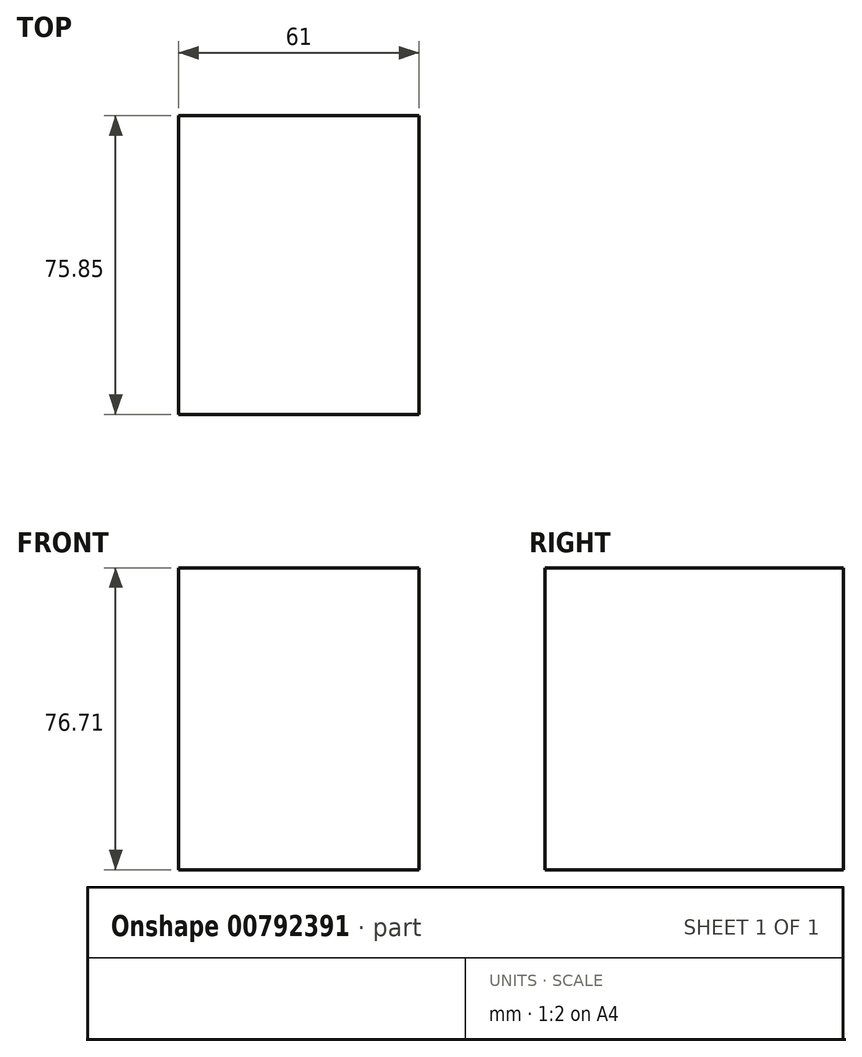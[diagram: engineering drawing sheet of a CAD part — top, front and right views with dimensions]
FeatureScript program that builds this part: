
annotation { "Feature Type Name" : "Feature", "Feature Type Description" : "" }
export const myFeature = defineFeature(function(context is Context, id is Id, definition is map)
    precondition{}
    {
        {
            var Q0;
            Q0=qCreatedBy(makeId("Top.planeOp"),FACE);
            var sketch = newSketch(context, id + "F0", { "sketchPlane" : qUnion([Q0])});
            skLineSegment(sketch, "E0.bottom", {"start": v(-26.76, -31.6) * mm, "end": v(34.24, -31.6) * mm});
            skLineSegment(sketch, "E0.top", {"start": v(-26.76, 44.24) * mm, "end": v(34.24, 44.24) * mm});
            skLineSegment(sketch, "E0.left", {"start": v(-26.76, -31.6) * mm, "end": v(-26.76, 44.24) * mm});
            skLineSegment(sketch, "E0.right", {"start": v(34.24, -31.6) * mm, "end": v(34.24, 44.24) * mm});
            skSolve(sketch);
        }
        {
            var Q0;
            Q0=makeQuery(id+"F0.imprint","IMPRINT",FACE,{"disambiguationData":[TD([[makeQuery(id+"F0.imprint","IMPRINT",EDGE,{"derivedFrom":sQuery(id+"F0.wireOp",EDGE,"E0.bottom")}),1.0]])]});
            extrude(context, id + "F1", {"entities" : qUnion([Q0]), "depth" : 76.7 * mm, "offsetDistance" : 25.4 * mm});
        }
    });
